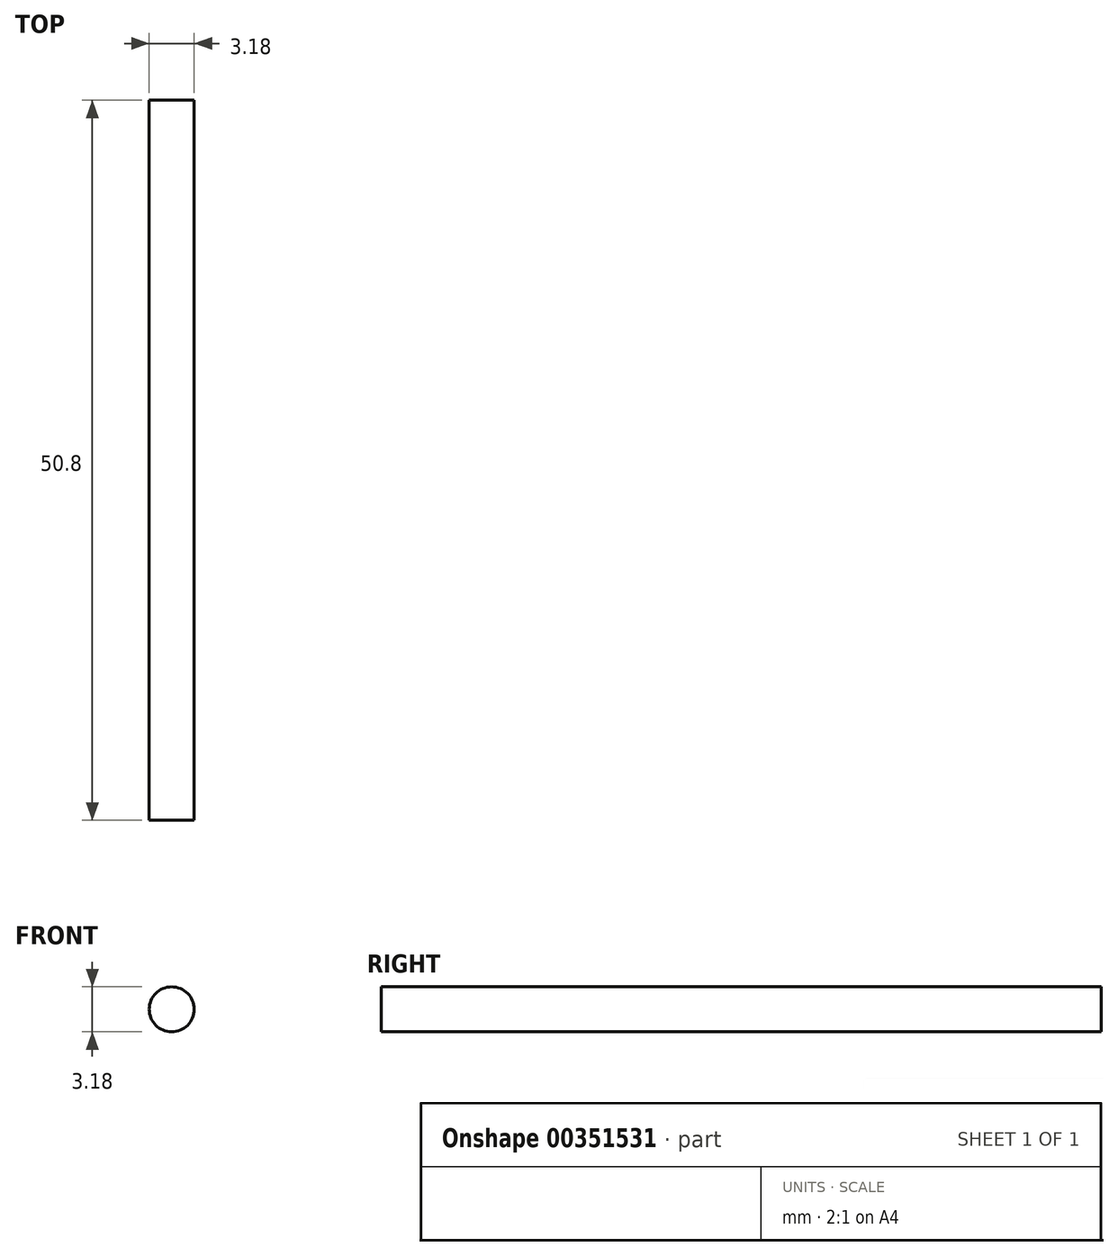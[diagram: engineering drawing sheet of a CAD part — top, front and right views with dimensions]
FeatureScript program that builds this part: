
annotation { "Feature Type Name" : "Feature", "Feature Type Description" : "" }
export const myFeature = defineFeature(function(context is Context, id is Id, definition is map)
    precondition{}
    {
        {
            var Q0;
            Q0=qCreatedBy(makeId("Front.planeOp"),FACE);
            var sketch = newSketch(context, id + "F0", { "sketchPlane" : qUnion([Q0])});
            skCircle(sketch, "E0", {"center": v(0, 0) * mm, "radius": 1.59 * mm});
            skSolve(sketch);
        }
        {
            var Q0;
            Q0 = qSketchRegion(id + "F0", true);
            extrude(context, id + "F1", {"entities" : qUnion([Q0]), "depth" : 50.8 * mm, "symmetric" : true});
        }
    });
